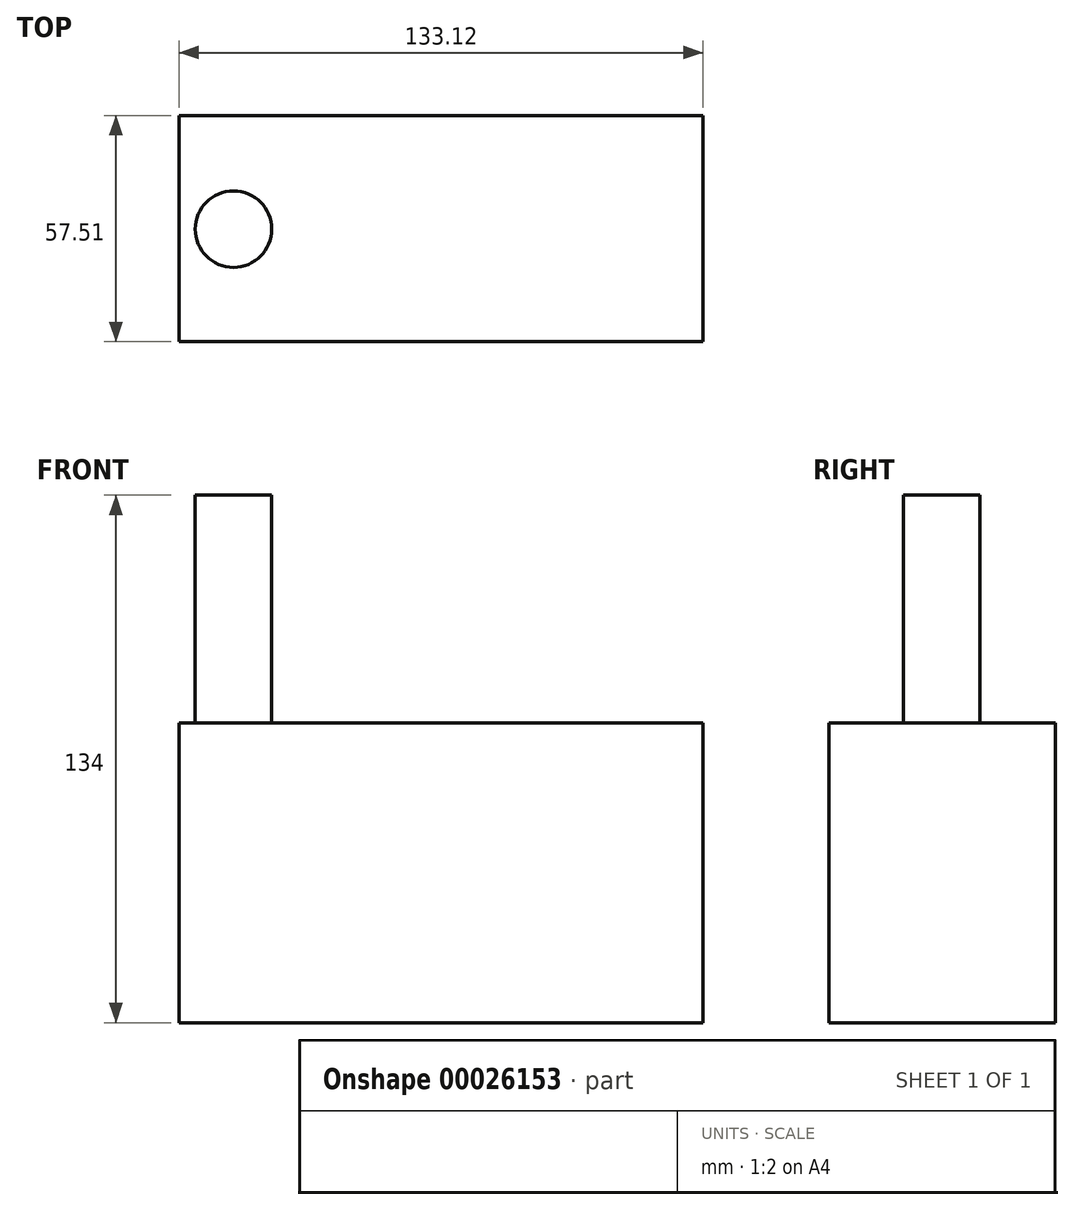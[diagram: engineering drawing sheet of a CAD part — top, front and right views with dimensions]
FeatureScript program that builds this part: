
annotation { "Feature Type Name" : "Feature", "Feature Type Description" : "" }
export const myFeature = defineFeature(function(context is Context, id is Id, definition is map)
    precondition{}
    {
        {
            var Q0;
            Q0=qCreatedBy(makeId("Top.planeOp"),FACE);
            var sketch = newSketch(context, id + "F0", { "sketchPlane" : qUnion([Q0])});
            skLineSegment(sketch, "E0.bottom", {"start": v(-66.96, 28.89) * mm, "end": v(66.16, 28.89) * mm});
            skLineSegment(sketch, "E0.top", {"start": v(-66.96, -28.62) * mm, "end": v(66.16, -28.62) * mm});
            skLineSegment(sketch, "E0.left", {"start": v(-66.96, 28.89) * mm, "end": v(-66.96, -28.62) * mm});
            skLineSegment(sketch, "E0.right", {"start": v(66.16, 28.89) * mm, "end": v(66.16, -28.62) * mm});
            skLineSegment(sketch, "E1.bottom", {"start": v(-66.96, -28.62) * mm, "end": v(-58.44, -28.62) * mm});
            skLineSegment(sketch, "E1.top", {"start": v(-66.96, -68.56) * mm, "end": v(-58.44, -68.56) * mm});
            skLineSegment(sketch, "E1.left", {"start": v(-66.96, -28.62) * mm, "end": v(-66.96, -68.56) * mm});
            skLineSegment(sketch, "E1.right", {"start": v(-58.44, -28.62) * mm, "end": v(-58.44, -68.56) * mm});
            skLineSegment(sketch, "E2.bottom", {"start": v(66.16, -28.62) * mm, "end": v(57.91, -28.62) * mm});
            skLineSegment(sketch, "E2.top", {"start": v(66.16, -68.56) * mm, "end": v(57.91, -68.56) * mm});
            skLineSegment(sketch, "E2.left", {"start": v(66.16, -28.62) * mm, "end": v(66.16, -68.56) * mm});
            skLineSegment(sketch, "E2.right", {"start": v(57.91, -28.62) * mm, "end": v(57.91, -68.56) * mm});
            skSolve(sketch);
        }
        {
            var Q0;
            Q0=makeQuery(id+"F0.imprint","IMPRINT",FACE,{"disambiguationData":[TD([[makeQuery(id+"F0.imprint","IMPRINT",EDGE,{"derivedFrom":sQuery(id+"F0.wireOp",EDGE,"E1.bottom")}),-1.0]])]});
            var Q1;
            Q1=makeQuery(id+"F0.imprint","IMPRINT",FACE,{"disambiguationData":[TD([[makeQuery(id+"F0.imprint","IMPRINT",EDGE,{"derivedFrom":sQuery(id+"F0.wireOp",EDGE,"E2.bottom")}),1.0]])]});
            var Q2;
            Q2=makeQuery(id+"F0.imprint","IMPRINT",FACE,{"disambiguationData":[TD([[makeQuery(id+"F0.imprint","IMPRINT",EDGE,{"derivedFrom":sQuery(id+"F0.wireOp",EDGE,"E0.bottom")}),-1.0]])]});
            extrude(context, id + "F1", {"entities" : qUnion([Q0, Q1, Q2]), "depth" : 25.4 * mm});
        }
        {
            var Q0;
            Q0=qCreatedBy(makeId("Top.planeOp"),FACE);
            var sketch = newSketch(context, id + "F2", { "sketchPlane" : qUnion([Q0])});
            skLineSegment(sketch, "E3", {"start": v(-29.16, 16.64) * mm, "end": v(-29.16, 2.8) * mm});
            skLineSegment(sketch, "E4", {"start": v(-20.37, 16.9) * mm, "end": v(-20.37, 2.8) * mm});
            skLineSegment(sketch, "E5", {"start": v(-20.37, 2.8) * mm, "end": v(-29.16, 2.8) * mm});
            skLineSegment(sketch, "E6", {"start": v(-29.16, 16.64) * mm, "end": v(-25.7, 16.9) * mm});
            skLineSegment(sketch, "E7", {"start": v(-25.7, 16.9) * mm, "end": v(-25.7, 24.63) * mm});
            skLineSegment(sketch, "E8", {"start": v(-25.7, 24.63) * mm, "end": v(-23.83, 24.63) * mm});
            skLineSegment(sketch, "E9", {"start": v(-23.83, 24.63) * mm, "end": v(-23.83, 17.17) * mm});
            skLineSegment(sketch, "E10", {"start": v(-23.83, 17.17) * mm, "end": v(-20.37, 16.9) * mm});
            skSolve(sketch);
        }
        {
            var Q0;
            Q0 = qSketchRegion(id + "F2", true);
            var Q1;
            Q1=makeQuery(id+"F1.opExtrude","CAP_FACE",FACE,{"disambiguationData":[OSD([sQuery(id+"F0.wireOp",EDGE,"E0.bottom"),sQuery(id+"F0.wireOp",EDGE,"E0.top"),sQuery(id+"F0.wireOp",EDGE,"E0.left"),sQuery(id+"F0.wireOp",EDGE,"E0.right"),sQuery(id+"F0.wireOp",EDGE,"E1.top"),sQuery(id+"F0.wireOp",EDGE,"E1.left"),sQuery(id+"F0.wireOp",EDGE,"E1.right"),sQuery(id+"F0.wireOp",EDGE,"E2.top"),sQuery(id+"F0.wireOp",EDGE,"E2.left"),sQuery(id+"F0.wireOp",EDGE,"E2.right")])],"isStart":false});
            extrude(context, id + "F3", {"entities" : qUnion([Q0, Q1]), "operationType" : NewBodyOperationType.ADD, "depth" : 25.4 * mm});
        }
        {
            var sketch = newSketch(context, id + "F4", { "sketchPlane" : qUnion([])});
            skLineSegment(sketch, "E11.bottom", {"start": v(-26.47, 12.6) * mm, "end": v(-16.4, 12.6) * mm});
            skLineSegment(sketch, "E11.top", {"start": v(-26.47, -3.96) * mm, "end": v(-16.4, -3.96) * mm});
            skLineSegment(sketch, "E11.left", {"start": v(-26.47, 12.6) * mm, "end": v(-26.47, -3.96) * mm});
            skLineSegment(sketch, "E11.right", {"start": v(-16.4, 12.6) * mm, "end": v(-16.4, -3.96) * mm});
            skLineSegment(sketch, "E12.bottom", {"start": v(-23.23, 22.67) * mm, "end": v(-21.43, 22.67) * mm});
            skLineSegment(sketch, "E12.top", {"start": v(-23.23, 12.6) * mm, "end": v(-21.43, 12.6) * mm});
            skLineSegment(sketch, "E12.left", {"start": v(-23.23, 22.67) * mm, "end": v(-23.23, 12.6) * mm});
            skLineSegment(sketch, "E12.right", {"start": v(-21.43, 22.67) * mm, "end": v(-21.43, 12.6) * mm});
            skCircle(sketch, "E13", {"center": v(-53.1, 0) * mm, "radius": 11.72 * mm});
            skCircle(sketch, "E14", {"center": v(0, -14.4) * mm, "radius": 12.36 * mm});
            skCircle(sketch, "E15", {"center": v(50.53, 0) * mm, "radius": 12.14 * mm});
            skCircle(sketch, "E16", {"center": v(0, 18) * mm, "radius": 10.47 * mm});
            skLineSegment(sketch, "E17", {"start": v(-45.18, -15.11) * mm, "end": v(-62.45, -15.11) * mm});
            skLineSegment(sketch, "E18", {"start": v(-45.54, -18.35) * mm, "end": v(-62.8, -18.35) * mm});
            skLineSegment(sketch, "E19", {"start": v(16.35, -8.63) * mm, "end": v(16.35, -22.67) * mm});
            skLineSegment(sketch, "E20", {"start": v(22.1, -23.03) * mm, "end": v(22.1, -8.63) * mm});
            skLineSegment(sketch, "E21", {"start": v(58.1, 17.27) * mm, "end": v(41.18, 17.27) * mm});
            skLineSegment(sketch, "E22", {"start": v(58.1, 23.03) * mm, "end": v(40.46, 23.03) * mm});
            skLineSegment(sketch, "E23", {"start": v(14.2, 24.47) * mm, "end": v(14.2, 13.67) * mm});
            skLineSegment(sketch, "E24", {"start": v(18.51, 25.55) * mm, "end": v(18.51, 13.67) * mm});
            skLineSegment(sketch, "E25.bottom", {"start": v(14.2, 6.84) * mm, "end": v(29.3, 6.84) * mm});
            skLineSegment(sketch, "E25.top", {"start": v(14.2, 0) * mm, "end": v(29.3, 0) * mm});
            skLineSegment(sketch, "E25.left", {"start": v(14.2, 6.84) * mm, "end": v(14.2, 0) * mm});
            skLineSegment(sketch, "E25.right", {"start": v(29.3, 6.84) * mm, "end": v(29.3, 0) * mm});
            skSolve(sketch);
        }
        {
            var Q0;
            Q0 = qSketchRegion(id + "F4", true);
            var Q1;
            Q1=makeQuery(id+"F3.opExtrude","CAP_FACE",FACE,{"disambiguationData":[OSD([sQuery(id+"F0.wireOp",EDGE,"E0.bottom"),sQuery(id+"F0.wireOp",EDGE,"E0.top"),sQuery(id+"F0.wireOp",EDGE,"E0.left"),sQuery(id+"F0.wireOp",EDGE,"E0.right"),sQuery(id+"F0.wireOp",EDGE,"E1.top"),sQuery(id+"F0.wireOp",EDGE,"E1.left"),sQuery(id+"F0.wireOp",EDGE,"E1.right"),sQuery(id+"F0.wireOp",EDGE,"E2.top"),sQuery(id+"F0.wireOp",EDGE,"E2.left"),sQuery(id+"F0.wireOp",EDGE,"E2.right")])],"isStart":false});
            extrude(context, id + "F5", {"entities" : qUnion([Q0, Q1]), "operationType" : NewBodyOperationType.ADD, "depth" : 25.4 * mm});
        }
        {
            var Q0;
            Q0=makeQuery(id+"F5.opExtrude","CAP_FACE",FACE,{"disambiguationData":[OSD([sQuery(id+"F0.wireOp",EDGE,"E0.bottom"),sQuery(id+"F0.wireOp",EDGE,"E0.top"),sQuery(id+"F0.wireOp",EDGE,"E0.left"),sQuery(id+"F0.wireOp",EDGE,"E0.right"),sQuery(id+"F0.wireOp",EDGE,"E1.top"),sQuery(id+"F0.wireOp",EDGE,"E1.left"),sQuery(id+"F0.wireOp",EDGE,"E1.right"),sQuery(id+"F0.wireOp",EDGE,"E2.top"),sQuery(id+"F0.wireOp",EDGE,"E2.left"),sQuery(id+"F0.wireOp",EDGE,"E2.right")])],"isStart":false});
            var sketch = newSketch(context, id + "F6", { "sketchPlane" : qUnion([Q0])});
            skCircle(sketch, "E26", {"center": v(-53.1, 0) * mm, "radius": 9.72 * mm});
            skSolve(sketch);
        }
        {
            var Q0;
            Q0=makeQuery(id+"F6.imprint","IMPRINT",FACE,{"disambiguationData":[TD([[makeQuery(id+"F6.imprint","IMPRINT",EDGE,{"derivedFrom":sQuery(id+"F6.wireOp",EDGE,"E26")}),1.0]])]});
            extrude(context, id + "F7", {"entities" : qUnion([Q0]), "operationType" : NewBodyOperationType.ADD, "depth" : 25.4 * mm});
        }
        {
            var Q0;
            Q0=makeQuery(id+"F7.opExtrude","CAP_FACE",FACE,{"disambiguationData":[OSD([sQuery(id+"F6.wireOp",EDGE,"E26")])],"isStart":false});
            extrude(context, id + "F8", {"entities" : qUnion([Q0]), "operationType" : NewBodyOperationType.ADD, "depth" : 25.4 * mm});
        }
        {
            var Q0;
            Q0=makeQuery(id+"F8.opExtrude","CAP_FACE",FACE,{"disambiguationData":[OSD([sQuery(id+"F6.wireOp",EDGE,"E26")])],"isStart":false});
            extrude(context, id + "F9", {"entities" : qUnion([Q0]), "operationType" : NewBodyOperationType.ADD, "depth" : 7 * mm});
        }
    });
